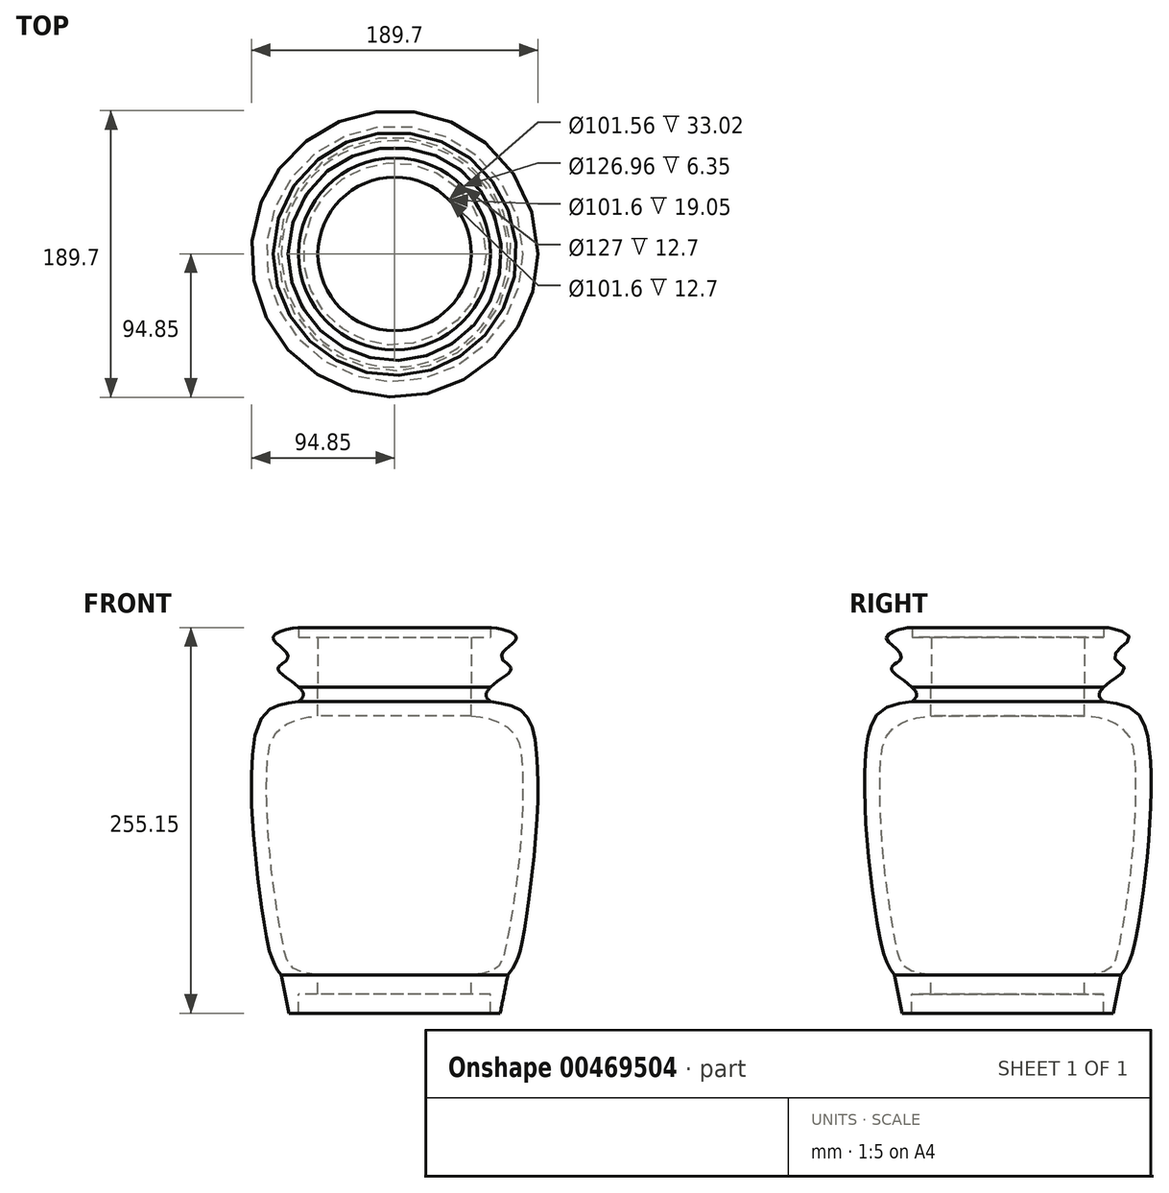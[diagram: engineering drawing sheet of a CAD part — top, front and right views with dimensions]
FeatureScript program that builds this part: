
annotation { "Feature Type Name" : "Feature", "Feature Type Description" : "" }
export const myFeature = defineFeature(function(context is Context, id is Id, definition is map)
    precondition{}
    {
        {
            var Q0;
            Q0=qCreatedBy(makeId("Front.planeOp"),FACE);
            var sketch = newSketch(context, id + "F0", { "sketchPlane" : qUnion([Q0])});
            skLineSegment(sketch, "E0", {"start": v(-50.8, 12.7) * mm, "end": v(-63.5, 12.7) * mm});
            skLineSegment(sketch, "E1", {"start": v(-63.5, 12.7) * mm, "end": v(-63.5, 0) * mm});
            skLineSegment(sketch, "E2", {"start": v(-63.5, 0) * mm, "end": v(-69.85, 0) * mm});
            skLineSegment(sketch, "E3", {"start": v(-69.85, 0) * mm, "end": v(-74.9, 25.3) * mm});
            skLineSegment(sketch, "E4", {"start": v(-50.8, 215.78) * mm, "end": v(-63.5, 215.78) * mm});
            skFitSpline(sketch, "E5", {"points": [v(-63.5, 206.13) * mm, v(-85.04, 199.2) * mm, v(-94.23, 169.15) * mm, v(-92.22, 104.17) * mm, v(-83.6, 44.06) * mm, v(-80.78, 35.23) * mm, v(-74.9, 25.3) * mm], "startDerivative": vector(-163.93, -21.92) * mm, "endDerivative": vector(82.33, -81.74) * mm});
            skLineSegment(sketch, "E6", {"start": v(-50.8, 215.78) * mm, "end": v(-50.8, 196.73) * mm});
            skLineSegment(sketch, "E7", {"start": v(-50.8, 12.7) * mm, "end": v(-50.8, 25.4) * mm});
            skFitSpline(sketch, "E8", {"points": [v(-50.8, 196.73) * mm, v(-65.55, 194.02) * mm, v(-79.36, 184.54) * mm, v(-84.44, 164.15) * mm, v(-82.4, 103.56) * mm, v(-73.67, 44.4) * mm, v(-67.38, 29.75) * mm, v(-50.8, 25.4) * mm], "startDerivative": vector(-131.5, -14.73) * mm, "endDerivative": vector(168.7, -19.08) * mm});
            skLineSegment(sketch, "E9", {"start": v(0, 215.56) * mm, "end": v(0, 0) * mm, "construction": true});
            skPoint(sketch, "E10", {"position": v(-84.44, 169.15) * mm});
            skFitSpline(sketch, "E11", {"points": [v(-63.5, 206.13) * mm, v(-60.45, 210.18) * mm, v(-63.5, 215.78) * mm], "startDerivative": vector(9.86, 8.92) * mm, "endDerivative": vector(-12.72, 11.47) * mm});
            skSolve(sketch);
        }
        {
            var Q0;
            Q0=makeQuery(id+"F0.imprint","IMPRINT",FACE,{"disambiguationData":[TD([[makeQuery(id+"F0.imprint","IMPRINT",EDGE,{"derivedFrom":sQuery(id+"F0.wireOp",EDGE,"E0")}),-1.0]])]});
            var Q1;
            Q1=sQuery(id+"F0.wireOp",EDGE,"E9");
            revolve(context, id + "F1", {"entities" : qUnion([Q0]), "axis" : qUnion([Q1]), "revolveType" : RevolveType.FULL});
        }
        {
            var Q0;
            Q0=makeQuery(id+"F0.imprint","IMPRINT",FACE,{"disambiguationData":[TD([[makeQuery(id+"F0.imprint","IMPRINT",EDGE,{"derivedFrom":sQuery(id+"F0.wireOp",EDGE,"E0")}),-1.0]])]});
            var sketch = newSketch(context, id + "F2", { "sketchPlane" : qUnion([Q0])});
            skLineSegment(sketch, "E12", {"start": v(-50.78, 215.78) * mm, "end": v(-63.5, 215.78) * mm});
            skLineSegment(sketch, "E13", {"start": v(-50.78, 215.78) * mm, "end": v(-50.78, 248.8) * mm});
            skLineSegment(sketch, "E14", {"start": v(-50.78, 248.8) * mm, "end": v(-63.48, 248.8) * mm});
            skLineSegment(sketch, "E15", {"start": v(-63.48, 248.8) * mm, "end": v(-63.48, 255.15) * mm});
            skFitSpline(sketch, "E16", {"points": [v(-63.48, 255.15) * mm, v(-80.43, 248.87) * mm, v(-73.9, 241.2) * mm, v(-70.97, 234.33) * mm, v(-77.16, 228.36) * mm, v(-71.42, 221.94) * mm, v(-63.5, 215.78) * mm], "startDerivative": vector(-84.6, 1.92) * mm, "endDerivative": vector(68.55, -64.83) * mm});
            skLineSegment(sketch, "E17", {"start": v(0, 216.23) * mm, "end": v(0, 269.87) * mm, "construction": true});
            skSolve(sketch);
        }
        {
            var Q0;
            Q0=makeQuery(id+"F2.imprint","IMPRINT",FACE,{"disambiguationData":[TD([[makeQuery(id+"F2.imprint","IMPRINT",EDGE,{"derivedFrom":sQuery(id+"F2.wireOp",EDGE,"E12")}),-1.0]])]});
            var Q1;
            Q1=sQuery(id+"F2.wireOp",EDGE,"E17");
            revolve(context, id + "F3", {"entities" : qUnion([Q0]), "axis" : qUnion([Q1]), "revolveType" : RevolveType.FULL});
        }
    });
